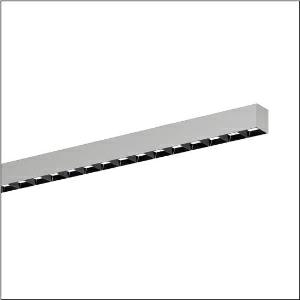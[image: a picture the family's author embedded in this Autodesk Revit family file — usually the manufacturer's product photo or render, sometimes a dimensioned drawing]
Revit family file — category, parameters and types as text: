
# Revit family: silica_r__21_51mx24dc3asb_5aec
name_source: partatom
category: Lighting Fixtures
units: mm (PartAtom-declared; Revit-internal decimal feet)

## family parameters
Cut with Voids When Loaded = No
Host = Face
Light Source = No
Part Type = Normal
Room Calculation Point = No
Round Connector Dimension = Use Diameter
Shared = No

## types (1)
- --- (1 x LED, 10800 lm, 79 W, 3000K)
    Apparent Load = 79 VA
    CIE Flux Codes = 74 94 99 100 100
    Color Rendering = 80
    Color Temperature = 3000K
    Default Elevation = 1800 mm
    Description = Silica® 21, office luminaire, primary light control with darklight reflector, of PMMA, black, CAT 2 (L<= 3000cd/m²), light emission: direct distribution, primary light characteristic: asymmetric, installation type: surface-mounted, LED, rated luminous flux: 10.800lm, luminous efficacy: 137lm/W, light colour: 830, colour temperature: 3000K, with terminal, 3+2-pole, max. 2.5mm², mains connection: 220..240V, AC, 50/60Hz, rated input power: 79W, luminaire housing, of aluminium, metallic grey (RAL 9006), length: 3.004mm, width: 53mm, height: 53mm, protection rating (complete): IP20, insulation class (complete): insulation class I (protective earthing), certification: CE, permissible operating ambient temperature: 0..+35°C, standard: EN 50419, packaging unit: 1 piece
    Height = 0 mm  [stored 0 ft]
    Lamp = 1 x LED
    Lamp Light Flux = 10800 lm
    Lamp Power = 79 W
    Lamp count = 1
    Length = 3004 mm
    Luminous efficacy = 137 lm/W
    Manufacturer = Siteco
    ModVariant = No
    Model = 51MX24DC3ASB
    Mounting Place = Ceiling
    Mounting Type = Recessed
    Number of Poles = 1
    OnlyDefault = Yes
    Power Factor = 1
    Product Name = Silica® 21
    Product group = office luminaire | ceiling recessed
    ProductGroupID = 401
    Protection Class = Protection class I
    Protection Degree = IP 20
    RLX_Detail_Level = 1
    RLX_Emergency_Light_Flux = 0 lm
    RLX_Emergency_Type = 0
    RLX_Emergency_Type_DB = No
    RlxData = <blob elided: 64509 chars, md5=5731e69a>
    Socket = socket
    Standby Power = 0 W
    System Light Flux = 10800 lm
    System Power = 79 W
    Type Comments = factory setting: luminous flux: 100 % | dim-lin: 254 | 448 mA
    Type Image = l_1313585.jpg
    URL = http://relux.com
    VarID = @adj_071425
    Voltage = 0 V
    Weight = 0.00 kg
    Width = 53 mm

note: [stored X ft] marks values corroborated as IEEE doubles in the binary element streams (Revit-internal decimal feet)

## geometry (parser evidence)
native form markers: Blend x4, Sweep x9
no freeform markers — native parametric forms only
